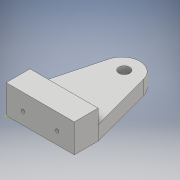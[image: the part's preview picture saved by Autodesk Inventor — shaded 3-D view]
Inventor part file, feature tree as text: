
AUTODESK INVENTOR PART (.ipt)
format: ipt  version: 2019 (Build 230136000, 136)  size: 128,000 bytes
history: native  units: mm
features: sketch x5, extrude x3
ambient origin geometry x8: Origin, YZ Plane, XZ Plane, XY Plane, X Axis, Y Axis, Z Axis, Center Point
bodies: Solid1 (feature_tree)
feature tree (8):
  sketch  "Sketch1"  dims[d9=4.2mm d10=0.0mm d11=4.2mm d12=0.0mm]
  sketch  "Sketch2"  dims[d13=1.0mm d14=1.0mm]
  sketch  "Sketch3"  dims[d15=5.5mm d16=0.0mm d17=7.0mm]
  extrude  "Extrusion1"  Depth=4.2mm TaperAngle=0.0deg
  extrude  "Extrusion2"  Depth=1.0mm
  extrude  "Extrusion3"  Depth=7.0mm
  sketch  "Sketch4"  dims[d18=6.999813mm]
  sketch  "Sketch5"  dims[d19=24.7mm d23=90.0deg d24=90.0deg d25=10.0mm d26=19.0mm d27=75.0deg d28=19.0mm d29=105.0deg d30=10.0mm d33=4.8mm d34=4.8mm]
